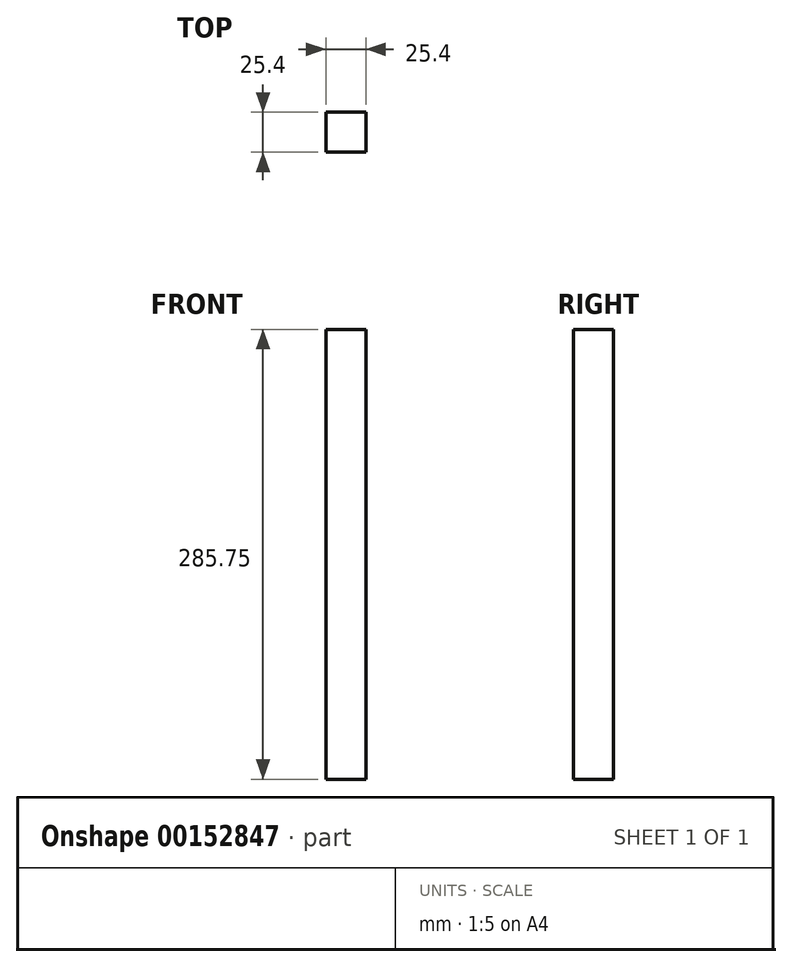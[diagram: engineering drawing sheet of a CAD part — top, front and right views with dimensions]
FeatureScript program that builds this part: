
annotation { "Feature Type Name" : "Feature", "Feature Type Description" : "" }
export const myFeature = defineFeature(function(context is Context, id is Id, definition is map)
    precondition{}
    {
        {
            var Q0;
            Q0=qCreatedBy(makeId("Top.planeOp"),FACE);
            var sketch = newSketch(context, id + "F0", { "sketchPlane" : qUnion([Q0])});
            skLineSegment(sketch, "E0.bottom", {"start": v(12.7, -12.7) * mm, "end": v(-12.7, -12.7) * mm});
            skLineSegment(sketch, "E0.top", {"start": v(12.7, 12.7) * mm, "end": v(-12.7, 12.7) * mm});
            skLineSegment(sketch, "E0.left", {"start": v(12.7, -12.7) * mm, "end": v(12.7, 12.7) * mm});
            skLineSegment(sketch, "E0.right", {"start": v(-12.7, -12.7) * mm, "end": v(-12.7, 12.7) * mm});
            skPoint(sketch, "E0.middle", {"position": v(0, 0) * mm});
            skSolve(sketch);
        }
        {
            var Q0;
            Q0=qSketchRegion(id+"F0",true);
            extrude(context, id + "F1", {"entities" : qUnion([Q0]), "depth" : 285.75 * mm});
        }
    });
